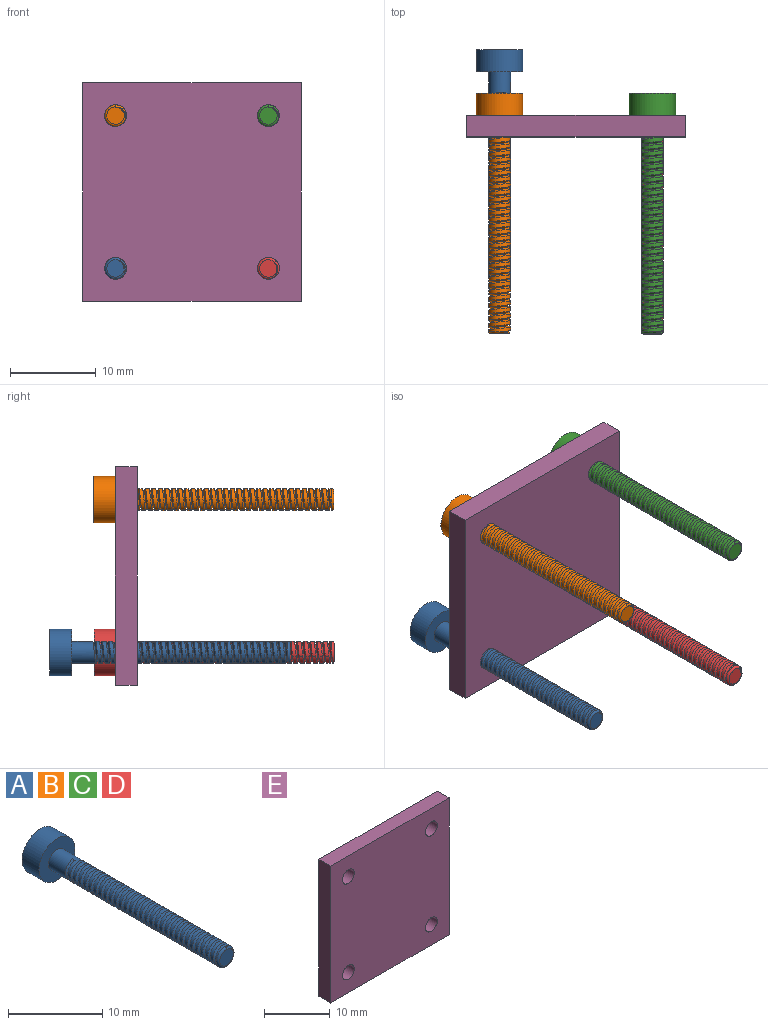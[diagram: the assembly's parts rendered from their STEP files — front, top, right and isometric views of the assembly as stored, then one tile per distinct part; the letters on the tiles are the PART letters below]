
ASSEMBLY  parts=5 mates=6
PART A: 46 faces, bbox 5.4x28.3x5.4 mm
  f0: plane 5.4x5.4mm, normal (0,1,0), area 17.3mm2, adj f37,f39,f40,f41,f42,f43,f44
  f1: plane 2.04x2.04mm, normal (0,-1,0), area 3.2mm2, adj f2,f34,f35
  f2: torus R=1.02mm, axis (0,-1,0), area 2.1mm2, adj f1,f3,f33,f34,f35
  f3: cylinder r=1.27mm len=2.54mm, axis (0,-1,0), area 2.4mm2, adj f2,f4,f33,f34
  f4: cylinder r=1.27mm len=2.54mm, axis (0,-1,0), area 3.3mm2, adj f3,f5,f33,f34
  f5: cylinder r=1.27mm len=2.54mm, axis (0,-1,0), area 3.3mm2, adj f4,f6,f33,f34
  f6: cylinder r=1.27mm len=2.54mm, axis (0,-1,0), area 3.3mm2, adj f5,f7,f33,f34
  f7: cylinder r=1.27mm len=2.54mm, axis (0,-1,0), area 3.3mm2, adj f6,f8,f33,f34
  f8: cylinder r=1.27mm len=2.54mm, axis (0,-1,0), area 3.3mm2, adj f7,f9,f33,f34
  f9: cylinder r=1.27mm len=2.54mm, axis (0,-1,0), area 3.3mm2, adj f8,f10,f33,f34
  f10: cylinder r=1.27mm len=2.54mm, axis (0,-1,0), area 3.3mm2, adj f9,f11,f33,f34
  f11: cylinder r=1.27mm len=2.54mm, axis (0,-1,0), area 3.3mm2, adj f10,f12,f33,f34
  f12: cylinder r=1.27mm len=2.54mm, axis (0,-1,0), area 3.3mm2, adj f11,f13,f33,f34
  f13: cylinder r=1.27mm len=2.54mm, axis (0,-1,0), area 3.3mm2, adj f12,f14,f33,f34
  f14: cylinder r=1.27mm len=2.54mm, axis (0,-1,0), area 3.3mm2, adj f13,f15,f33,f34
  f15: cylinder r=1.27mm len=2.54mm, axis (0,-1,0), area 3.3mm2, adj f14,f16,f33,f34
  f16: cylinder r=1.27mm len=2.54mm, axis (0,-1,0), area 3.3mm2, adj f15,f17,f33,f34
  f17: cylinder r=1.27mm len=2.54mm, axis (0,-1,0), area 3.3mm2, adj f16,f18,f33,f34
  f18: cylinder r=1.27mm len=2.54mm, axis (0,-1,0), area 3.3mm2, adj f17,f19,f33,f34
  f19: cylinder r=1.27mm len=2.54mm, axis (0,-1,0), area 3.3mm2, adj f18,f20,f33,f34
  f20: cylinder r=1.27mm len=2.54mm, axis (0,-1,0), area 3.3mm2, adj f19,f21,f33,f34
  f21: cylinder r=1.27mm len=2.54mm, axis (0,-1,0), area 3.3mm2, adj f20,f22,f33,f34
  f22: cylinder r=1.27mm len=2.54mm, axis (0,-1,0), area 3.3mm2, adj f21,f23,f33,f34
  f23: cylinder r=1.27mm len=2.54mm, axis (0,-1,0), area 3.3mm2, adj f22,f24,f33,f34
  f24: cylinder r=1.27mm len=2.54mm, axis (0,-1,0), area 3.3mm2, adj f23,f25,f33,f34
  f25: cylinder r=1.27mm len=2.54mm, axis (0,-1,0), area 3.3mm2, adj f24,f26,f33,f34
  f26: cylinder r=1.27mm len=2.54mm, axis (0,-1,0), area 3.3mm2, adj f25,f27,f33,f34
  f27: cylinder r=1.27mm len=2.54mm, axis (0,-1,0), area 3.3mm2, adj f26,f28,f33,f34
  f28: cylinder r=1.27mm len=2.54mm, axis (0,-1,0), area 3.3mm2, adj f27,f29,f33,f34
  f29: cylinder r=1.27mm len=2.54mm, axis (0,-1,0), area 3.3mm2, adj f28,f30,f33,f34
  f30: cylinder r=1.27mm len=2.54mm, axis (0,-1,0), area 3.3mm2, adj f29,f31,f33,f34
  f31: cylinder r=1.27mm len=2.54mm, axis (0,-1,0), area 3.3mm2, adj f30,f32,f33,f34
  f32: cylinder r=1.27mm len=3.46mm, axis (0,-1,0), area 23.4mm2, adj f31,f33,f34,f36,f38
  f33: bspline ~23.24x3.76mm, area 73.2mm2, adj f2,f3,f4,f5,f6,f7,f8,f9
  f34: bspline ~23.24x3.76mm, area 73mm2, adj f1,f2,f3,f4,f5,f6,f7,f8
  f35: plane 0.28x0.16mm, normal (1,0,0), area 0mm2, adj f1,f2,f33
  f36: plane 0.35x0.3mm, normal (-1,0,0), area 0.1mm2, adj f32,f33,f34
  f37: cylinder r=2.7mm len=5.4mm, axis (0,-1,0), area 43.1mm2, adj f0,f38
  f38: plane 5.4x5.4mm, normal (0,-1,0), area 17.8mm2, adj f32,f37
  f39: plane 1.4x1.27mm, normal (0.3,0,-0.95), area 1.9mm2, adj f0,f40,f44,f45
  f40: plane 1.27x1.08mm, normal (-0.68,0,-0.74), area 1.9mm2, adj f0,f39,f41,f45
  f41: plane 1.43x1.27mm, normal (-0.98,0,0.22), area 1.9mm2, adj f0,f40,f42,f45
  f42: plane 1.4x1.27mm, normal (-0.3,0,0.95), area 1.9mm2, adj f0,f41,f43,f45
  f43: plane 1.27x1.08mm, normal (0.68,0,0.74), area 1.9mm2, adj f0,f42,f44,f45
  f44: plane 1.43x1.27mm, normal (0.98,0,-0.22), area 1.9mm2, adj f0,f39,f43,f45
  f45: plane 2.86x2.8mm, normal (0,1,0), area 5.6mm2, adj f39,f40,f41,f42,f43,f44
PART B: same geometry as A
PART C: same geometry as A
PART D: same geometry as A
PART E: 10 faces, bbox 25.4x2.5x25.4 mm
  f0: plane 25.4x2.54mm, normal (-1,0,0), area 64.5mm2, adj f1,f4,f8,f9
  f1: plane 25.4x2.54mm, normal (0,0,-1), area 64.5mm2, adj f0,f2,f8,f9
  f2: plane 25.4x2.54mm, normal (1,0,0), area 64.5mm2, adj f1,f4,f8,f9
  f3: cylinder r=1.27mm len=2.54mm, axis (0,1,0), area 20.3mm2, adj f8,f9
  f4: plane 25.4x2.54mm, normal (0,0,1), area 64.5mm2, adj f0,f2,f8,f9
  f5: cylinder r=1.27mm len=2.54mm, axis (0,1,0), area 20.3mm2, adj f8,f9
  f6: cylinder r=1.27mm len=2.54mm, axis (0,1,0), area 20.3mm2, adj f8,f9
  f7: cylinder r=1.27mm len=2.54mm, axis (0,1,0), area 20.3mm2, adj f8,f9
  f8: plane 25.4x25.4mm, normal (0,-1,0), area 624.9mm2, adj f0,f1,f2,f3,f4,f5,f6,f7
  f9: plane 25.4x25.4mm, normal (0,1,0), area 624.9mm2, adj f0,f1,f2,f3,f4,f5,f6,f7
PLACE A rot(axis=(0,1,0),31.3deg) t=(10.32,-20.77,-12.15)mm
PLACE B t=(10.32,-25.87,5.63)mm
PLACE C t=(28.1,-25.87,5.63)mm
PLACE D rot(axis=(0,1,0),45.7deg) t=(28.1,-25.91,-12.15)mm
PLACE E t=(19.21,-0.47,-3.26)mm fixed
MATE cylindrical C.f2 <-> E.f6  axis (0,-1,0) through (28.1,-25.87,5.63)mm
MATE cylindrical B.f2 <-> E.f5  axis (0,-1,0) through (10.32,-25.87,5.63)mm
MATE fastened C.f2 <-> E.f6  axis (0,-1,0) through (28.1,-0.47,5.63)mm
MATE cylindrical A.f2 <-> E.f7  axis (0,-1,0) through (10.32,-20.77,-12.15)mm
MATE fastened B.f2 <-> E.f5  axis (0,-1,0) through (10.32,-0.47,5.63)mm
MATE cylindrical D.f2 <-> E.f3  axis (0,-1,0) through (28.1,-25.91,-12.15)mm
